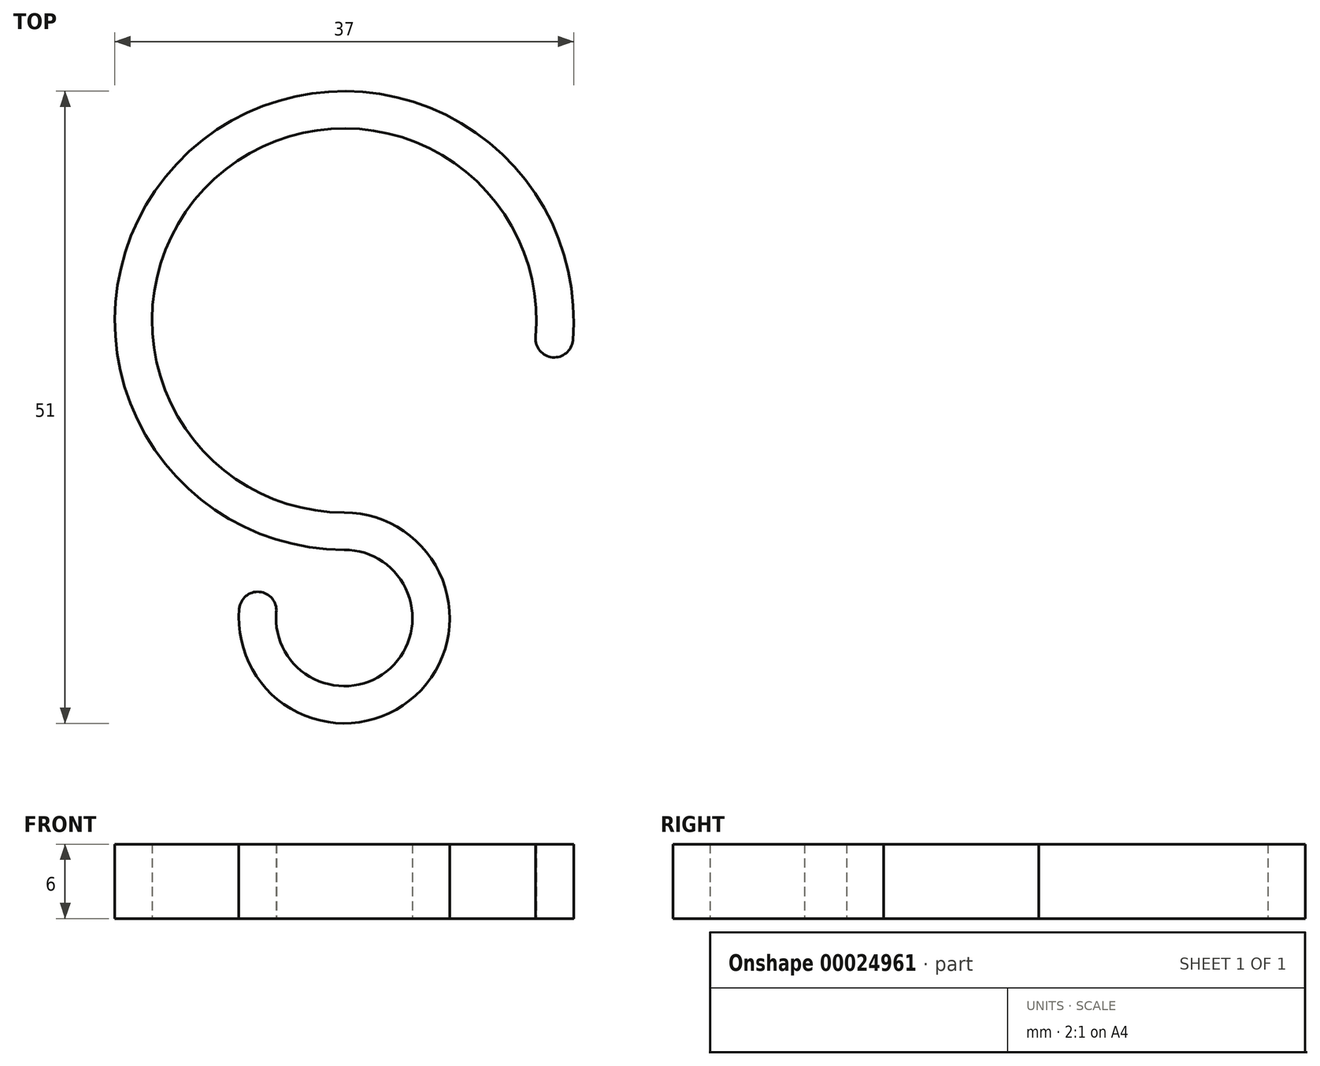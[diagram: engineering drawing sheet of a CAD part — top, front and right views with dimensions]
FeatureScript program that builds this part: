
annotation { "Feature Type Name" : "Feature", "Feature Type Description" : "" }
export const myFeature = defineFeature(function(context is Context, id is Id, definition is map)
    precondition{}
    {
        {
            var Q0;
            Q0=qCreatedBy(makeId("Top.planeOp"),FACE);
            var sketch = newSketch(context, id + "F0", { "sketchPlane" : qUnion([Q0])});
            skArc(sketch, "E0", {"start": v(-8.47, 0.74) * mm, "mid": v(5.74, -6.27) * mm, "end": v(0, 8.5) * mm});
            skArc(sketch, "E1", {"start": v(18.43, 22.39) * mm, "mid": v(-12.5, 37.64) * mm, "end": v(0, 5.5) * mm});
            skArc(sketch, "E2", {"start": v(-5.48, 0.48) * mm, "mid": v(3.72, -4.06) * mm, "end": v(0, 5.5) * mm});
            skArc(sketch, "E3", {"start": v(15.44, 22.65) * mm, "mid": v(-10.47, 35.43) * mm, "end": v(0, 8.5) * mm});
            skLineSegment(sketch, "E4", {"start": v(5.5, 0) * mm, "end": v(8.5, 0) * mm, "construction": true});
            skLineSegment(sketch, "E5", {"start": v(0, 24) * mm, "end": v(0, 0) * mm, "construction": true});
            skLineSegment(sketch, "E6", {"start": v(0, 24) * mm, "end": v(18.43, 22.39) * mm, "construction": true});
            skLineSegment(sketch, "E7", {"start": v(0, 0) * mm, "end": v(-8.47, 0.74) * mm, "construction": true});
            skLineSegment(sketch, "E8", {"start": v(18.43, 22.39) * mm, "end": v(15.44, 22.65) * mm, "construction": true});
            skLineSegment(sketch, "E9", {"start": v(-8.47, 0.74) * mm, "end": v(-5.48, 0.48) * mm, "construction": true});
            skArc(sketch, "E10", {"start": v(15.44, 22.65) * mm, "mid": v(16.8, 21.02) * mm, "end": v(18.43, 22.39) * mm});
            skArc(sketch, "E11", {"start": v(-5.48, 0.48) * mm, "mid": v(-6.84, 2.1) * mm, "end": v(-8.47, 0.74) * mm});
            skSolve(sketch);
        }
        {
            var Q0;
            Q0=makeQuery(id+"F0.imprint","IMPRINT",FACE,{"disambiguationData":[TD([[makeQuery(id+"F0.imprint","IMPRINT",EDGE,{"derivedFrom":sQuery(id+"F0.wireOp",EDGE,"E0")}),1.0]])]});
            extrude(context, id + "F1", {"entities" : qUnion([Q0]), "depth" : 6 * mm});
        }
    });
